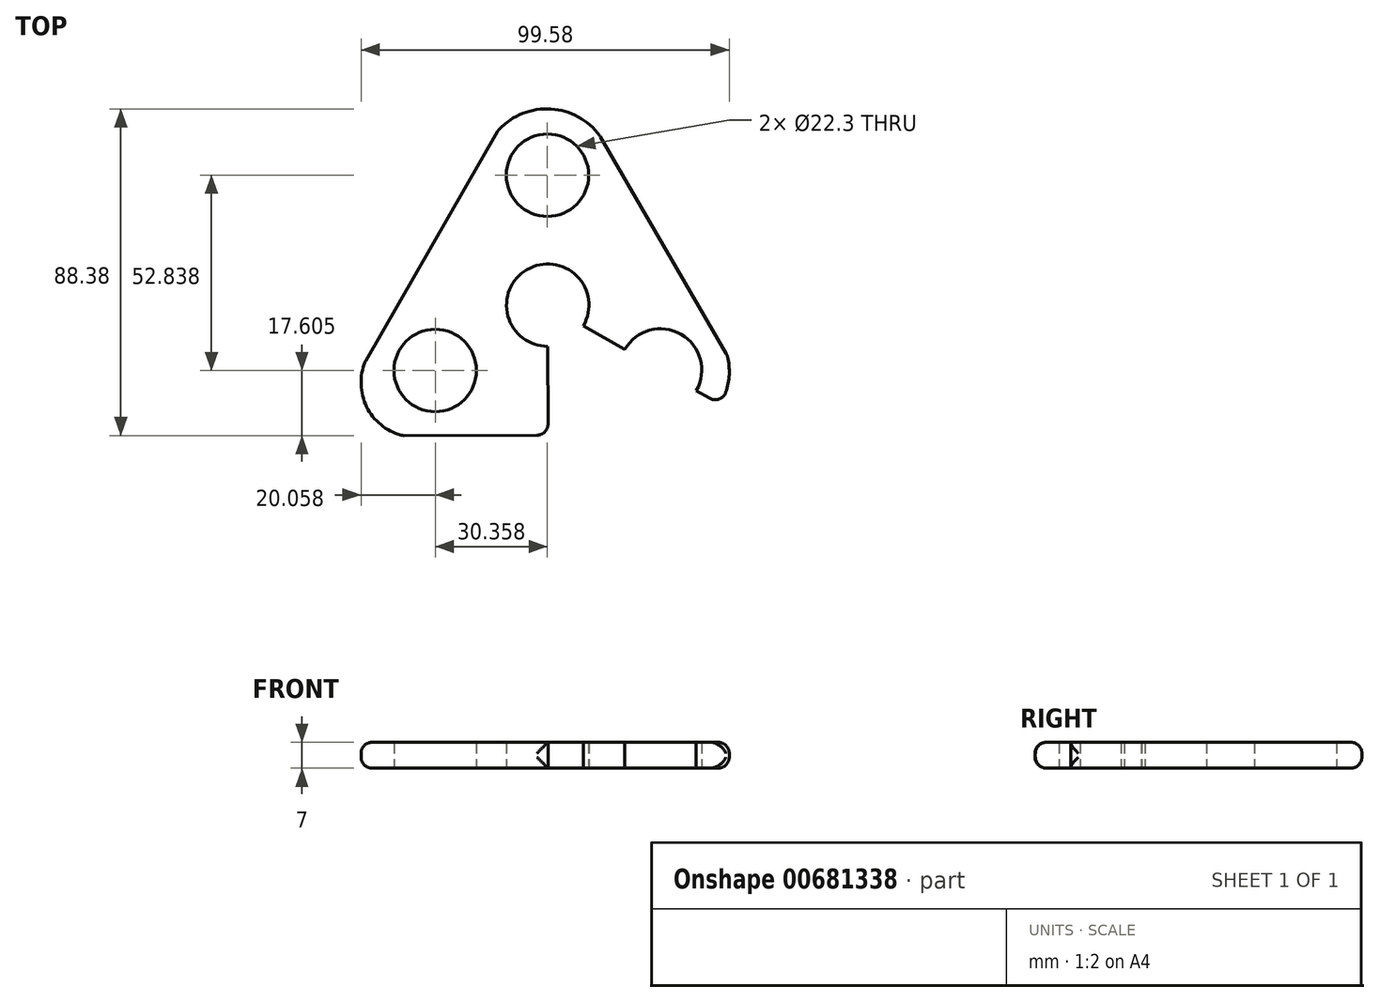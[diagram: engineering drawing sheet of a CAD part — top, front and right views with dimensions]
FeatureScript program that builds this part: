
annotation { "Feature Type Name" : "Feature", "Feature Type Description" : "" }
export const myFeature = defineFeature(function(context is Context, id is Id, definition is map)
    precondition{}
    {
        {
            var Q0;
            Q0=qCreatedBy(makeId("Top.planeOp"),FACE);
            var sketch = newSketch(context, id + "F0", { "sketchPlane" : qUnion([Q0])});
            skCircle(sketch, "E0", {"center": v(0, 0) * mm, "radius": 11.15 * mm});
            skCircle(sketch, "E1.cCircle", {"center": v(0, 0) * mm, "radius": 35.18 * mm, "construction": true});
            skLineSegment(sketch, "E1.0", {"start": v(7.4, 69.97) * mm, "end": v(56.9, -41.4) * mm});
            skLineSegment(sketch, "E1.1", {"start": v(56.9, -41.4) * mm, "end": v(-64.3, -28.58) * mm});
            skLineSegment(sketch, "E1.2", {"start": v(-64.3, -28.58) * mm, "end": v(7.4, 69.97) * mm});
            skPoint(sketch, "E1.0.midPoint", {"position": v(32.15, 14.29) * mm});
            skLineSegment(sketch, "E2", {"start": v(0, 0) * mm, "end": v(7.4, 69.97) * mm});
            skLineSegment(sketch, "E3", {"start": v(0, 0) * mm, "end": v(56.9, -41.4) * mm});
            skLineSegment(sketch, "E4", {"start": v(0, 0) * mm, "end": v(-64.3, -28.58) * mm});
            skCircle(sketch, "E5", {"center": v(-32.15, -14.29) * mm, "radius": 11.15 * mm});
            skCircle(sketch, "E6", {"center": v(3.7, 34.99) * mm, "radius": 11.15 * mm});
            skCircle(sketch, "E7", {"center": v(28.45, -20.7) * mm, "radius": 11.15 * mm});
            skArc(sketch, "E8", {"start": v(-50.62, -9.78) * mm, "mid": v(-50.03, -25.23) * mm, "end": v(-35.93, -31.58) * mm});
            skArc(sketch, "E9", {"start": v(18.98, 43.92) * mm, "mid": v(2.7, 52.93) * mm, "end": v(-12.66, 42.4) * mm});
            skArc(sketch, "E10", {"start": v(30.64, -38.62) * mm, "mid": v(45.51, -28.26) * mm, "end": v(43.08, -10.3) * mm});
            skLineSegment(sketch, "E11", {"start": v(-3.7, -34.99) * mm, "end": v(7.4, 69.97) * mm});
            skSolve(sketch);
        }
        {
            var Q0;
            {var subQ3=sQuery(id+"F0.wireOp",EDGE,"E2");var subQ5=sQuery(id+"F0.wireOp",EDGE,"E0");var subQ6=makeQuery(id+"F0.imprint","INTERSECT",VERTEX,{"derivedFrom":[subQ5,subQ3]});Q0=makeQuery(id+"F0.imprint","IMPRINT",FACE,{"disambiguationData":[TD([[makeQuery(id+"F0.imprint","IMPRINT",EDGE,{"disambiguationData":[TD([[subQ6,1.0]])],"derivedFrom":subQ5}),-1.0]])]});}
            var Q1;
            {var subQ3=sQuery(id+"F0.wireOp",EDGE,"E4");var subQ15=sQuery(id+"F0.wireOp",EDGE,"E0");var subQ16=makeQuery(id+"F0.imprint","INTERSECT",VERTEX,{"derivedFrom":[subQ15,subQ3]});Q1=makeQuery(id+"F0.imprint","IMPRINT",FACE,{"disambiguationData":[TD([[makeQuery(id+"F0.imprint","IMPRINT",EDGE,{"disambiguationData":[TD([[subQ16,1.0]])],"derivedFrom":subQ15}),-1.0]])]});}
            var Q2;
            {var subQ1=sQuery(id+"F0.wireOp",EDGE,"E4");var subQ7=sQuery(id+"F0.wireOp",EDGE,"E0");var subQ8=makeQuery(id+"F0.imprint","INTERSECT",VERTEX,{"derivedFrom":[subQ7,subQ1]});Q2=makeQuery(id+"F0.imprint","IMPRINT",FACE,{"disambiguationData":[TD([[makeQuery(id+"F0.imprint","IMPRINT",EDGE,{"disambiguationData":[TD([[subQ8,-1.0]])],"derivedFrom":subQ7}),-1.0]])]});}
            var Q3;
            {var subQ0=sQuery(id+"F0.wireOp",EDGE,"E11");var subQ1=sQuery(id+"F0.wireOp",EDGE,"E0");var subQ2=makeQuery(id+"F0.imprint","INTERSECT",VERTEX,{"disambiguationData":[OD(0.0)],"derivedFrom":[subQ1,subQ0]});Q3=makeQuery(id+"F0.imprint","IMPRINT",FACE,{"disambiguationData":[TD([[makeQuery(id+"F0.imprint","IMPRINT",EDGE,{"disambiguationData":[TD([[subQ2,1.0]])],"derivedFrom":subQ1}),-1.0]])]});}
            extrude(context, id + "F1", {"entities" : qUnion([Q0, Q1, Q2, Q3]), "depth" : 7 * mm, "offsetDistance" : 25 * mm});
        }
        {
            var Q0;
            Q0=makeQuery(id+"F1.opExtrude","CAP_EDGE",EDGE,{"disambiguationData":[OSD([sQuery(id+"F0.wireOp",EDGE,"E8")])],"isStart":false});
            var Q1;
            Q1=makeQuery(id+"F1.opExtrude","SWEPT_FACE",FACE,{"disambiguationData":[OSD([sQuery(id+"F0.wireOp",EDGE,"E8")])]});
            var Q2;
            Q2=makeQuery(id+"F1.opExtrude","SWEPT_FACE",FACE,{"disambiguationData":[OSD([sQuery(id+"F0.wireOp",EDGE,"E1.1")])]});
            var Q3;
            Q3=makeQuery(id+"F1.opExtrude","SWEPT_FACE",FACE,{"disambiguationData":[OSD([sQuery(id+"F0.wireOp",EDGE,"E10")])]});
            var Q4;
            Q4=makeQuery(id+"F1.opExtrude","SWEPT_FACE",FACE,{"disambiguationData":[OSD([sQuery(id+"F0.wireOp",EDGE,"E1.0")])]});
            var Q5;
            Q5=makeQuery(id+"F1.opExtrude","SWEPT_FACE",FACE,{"disambiguationData":[OSD([sQuery(id+"F0.wireOp",EDGE,"E9")])]});
            var Q6;
            Q6=makeQuery(id+"F1.opExtrude","SWEPT_FACE",FACE,{"disambiguationData":[OSD([sQuery(id+"F0.wireOp",EDGE,"E1.2")])]});
            fillet(context, id + "F2", {"entities" : qUnion([Q0, Q1, Q2, Q3, Q4, Q5, Q6]), "radius" : 3 * mm, "tangentPropagation" : true, "allowEdgeOverflow" : false});
        }
        {
            var Q0;
            Q0=makeQuery(id+"F1.opExtrude","SWEPT_BODY",BODY,{"disambiguationData":[OSD([sQuery(id+"F0.wireOp",EDGE,"E0"),sQuery(id+"F0.wireOp",EDGE,"E1.0"),sQuery(id+"F0.wireOp",EDGE,"E1.1"),sQuery(id+"F0.wireOp",EDGE,"E1.2"),sQuery(id+"F0.wireOp",EDGE,"E5"),sQuery(id+"F0.wireOp",EDGE,"E6"),sQuery(id+"F0.wireOp",EDGE,"E7"),sQuery(id+"F0.wireOp",EDGE,"E8"),sQuery(id+"F0.wireOp",EDGE,"E9"),sQuery(id+"F0.wireOp",EDGE,"E10")])]});
            var Q1;
            Q1=makeQuery(id+"F1.opExtrude","CAP_EDGE",EDGE,{"disambiguationData":[OSD([sQuery(id+"F0.wireOp",EDGE,"E0")])],"isStart":false});
            transform(context, id + "F3", {"entities" : qUnion([Q0]), "transformType" : TransformType.ROTATION, "transformAxis" : qUnion([Q1]), "angle" : 6.16 * degree, "makeCopy" : false});
        }
    });
